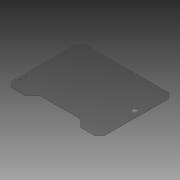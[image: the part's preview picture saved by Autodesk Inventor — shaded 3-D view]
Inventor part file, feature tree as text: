
AUTODESK INVENTOR PART (.ipt)
format: ipt  version: 2015 (Build 190159000, 159)  size: 202,752 bytes
history: native  units: mm
features: extrude x2, hole x1, chamfer x1, other x1, reference x1
ambient origin geometry x8: Origin, YZ Plane, XZ Plane, XY Plane, X Axis, Y Axis, Z Axis, Center Point
bodies: Solid1 (feature_tree)
feature tree (6):
  extrude  "Extrusión1"  Depth=3.0mm TaperAngle=0.0deg
  hole  "Agujero1"  [1 undecoded]
  chamfer  "Chaflán1"  Distance=0.5mm Angle=45.0deg
  extrude  "Extrusión2"  Depth=20.1mm
  other  "Eje de trabajo1"
  reference  "Referencia1"
note: 1 required parameter value undecoded (feature->parameter linkage not recoverable at this tier; creation-order binding heuristic only, values carry confidence <= 0.55)
